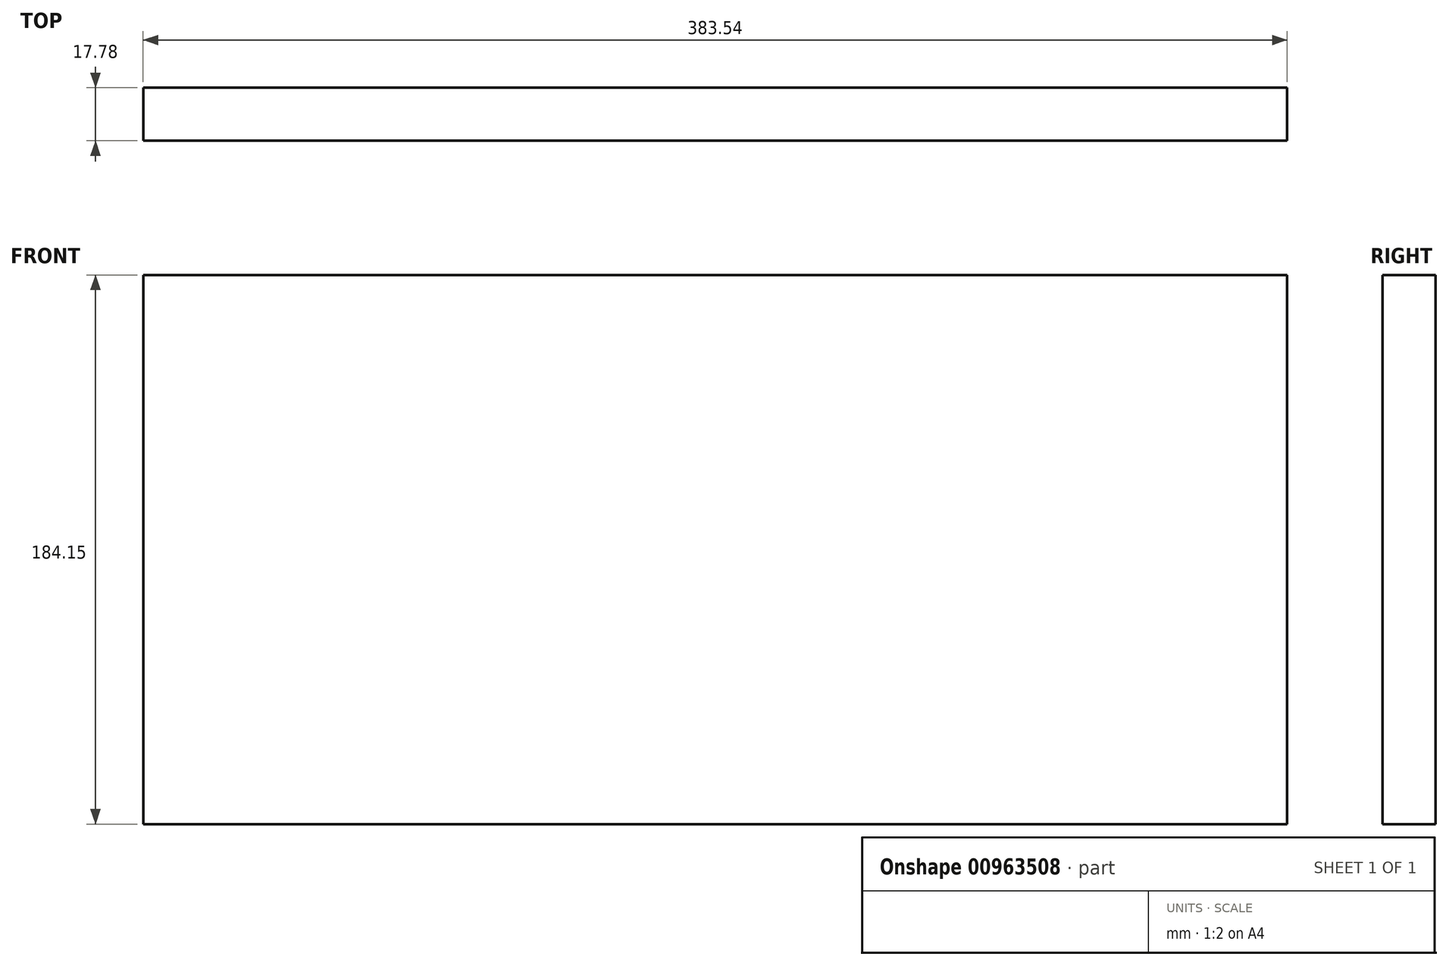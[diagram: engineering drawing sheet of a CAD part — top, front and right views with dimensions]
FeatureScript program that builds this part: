
annotation { "Feature Type Name" : "Feature", "Feature Type Description" : "" }
export const myFeature = defineFeature(function(context is Context, id is Id, definition is map)
    precondition{}
    {
        {
            var Q0;
            Q0=qCreatedBy(makeId("Front.planeOp"),FACE);
            var sketch = newSketch(context, id + "F0", { "sketchPlane" : qUnion([Q0])});
            skLineSegment(sketch, "E0.bottom", {"start": v(19.4, 7.17) * mm, "end": v(-364.15, 7.17) * mm});
            skLineSegment(sketch, "E0.top", {"start": v(19.4, 191.32) * mm, "end": v(-364.15, 191.32) * mm});
            skLineSegment(sketch, "E0.left", {"start": v(19.4, 7.17) * mm, "end": v(19.4, 191.32) * mm});
            skLineSegment(sketch, "E0.right", {"start": v(-364.15, 7.17) * mm, "end": v(-364.15, 191.32) * mm});
            skPoint(sketch, "E0.middle", {"position": v(-172.38, 99.25) * mm});
            skSolve(sketch);
        }
        {
            var Q0;
            Q0=makeQuery(id+"F0.imprint","IMPRINT",FACE,{"disambiguationData":[TD([[makeQuery(id+"F0.imprint","IMPRINT",EDGE,{"derivedFrom":sQuery(id+"F0.wireOp",EDGE,"E0.bottom")}),-1.0]])]});
            extrude(context, id + "F1", {"entities" : qUnion([Q0]), "depth" : 17.78 * mm, "offsetDistance" : 25.4 * mm});
        }
    });
